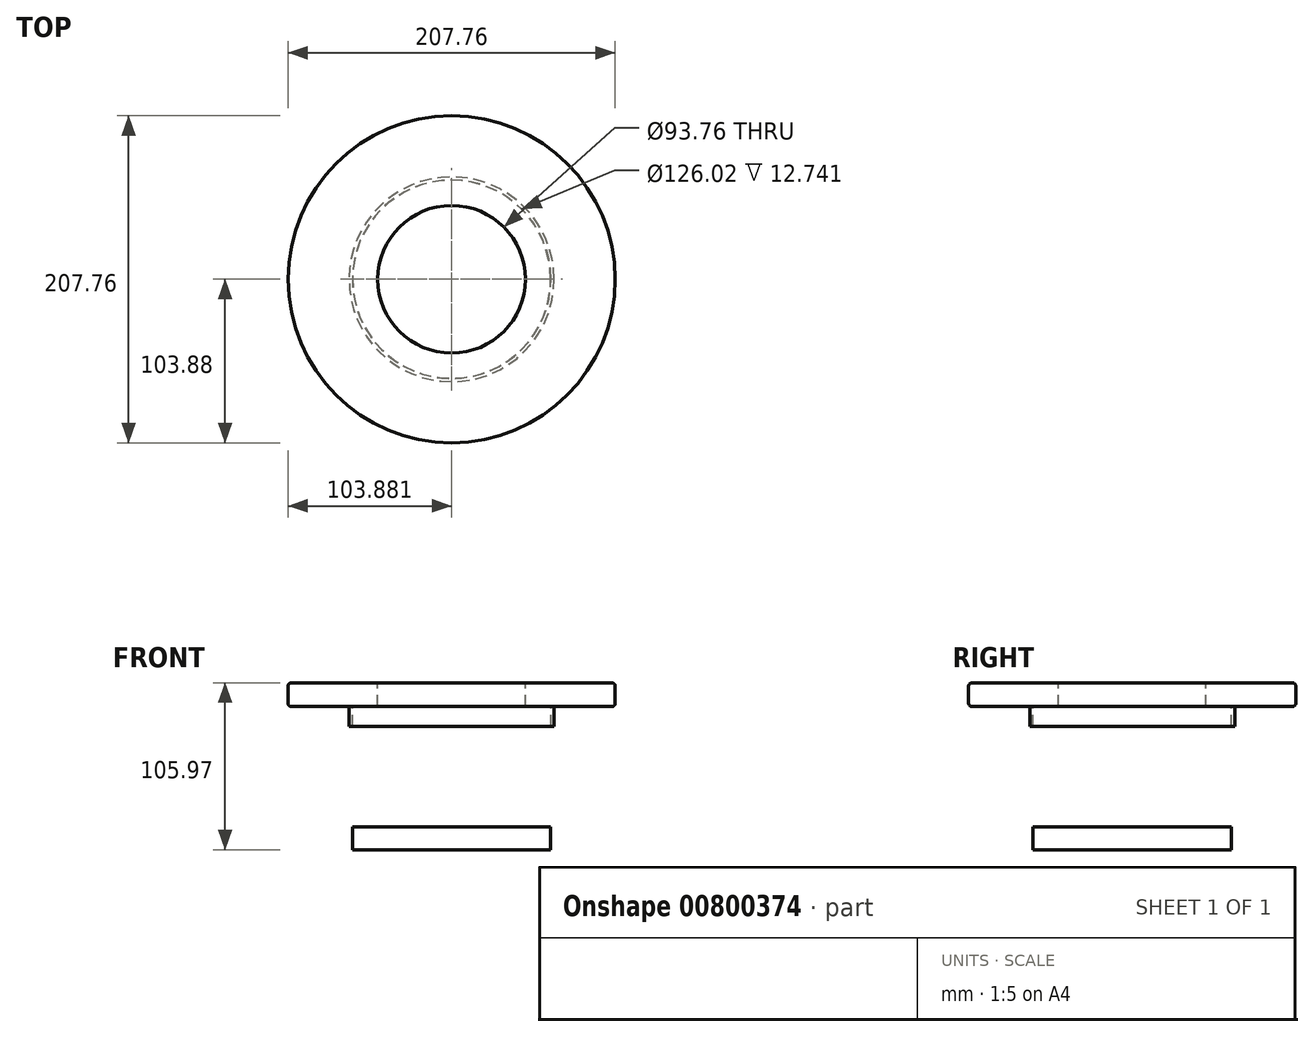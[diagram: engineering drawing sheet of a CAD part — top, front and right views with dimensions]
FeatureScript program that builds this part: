
annotation { "Feature Type Name" : "Feature", "Feature Type Description" : "" }
export const myFeature = defineFeature(function(context is Context, id is Id, definition is map)
    precondition{}
    {
        {
            var Q0;
            Q0=qCreatedBy(makeId("Front.planeOp"),FACE);
            var sketch = newSketch(context, id + "F0", { "sketchPlane" : qUnion([Q0])});
            skLineSegment(sketch, "E0.bottom", {"start": v(-44.86, 251.82) * mm, "end": v(-83.94, 251.82) * mm});
            skLineSegment(sketch, "E0.top", {"start": v(-44.86, 472.17) * mm, "end": v(-83.94, 472.17) * mm});
            skLineSegment(sketch, "E0.left", {"start": v(-44.86, 251.82) * mm, "end": v(-44.86, 472.17) * mm});
            skLineSegment(sketch, "E0.right", {"start": v(-83.94, 251.82) * mm, "end": v(-83.94, 472.17) * mm});
            skPoint(sketch, "E0.middle", {"position": v(-64.4, 362) * mm});
            skLineSegment(sketch, "E1.bottom", {"start": v(-7.4, 22.52) * mm, "end": v(-64.41, 22.52) * mm});
            skLineSegment(sketch, "E1.top", {"start": v(-7.4, 37.48) * mm, "end": v(-64.41, 37.48) * mm});
            skLineSegment(sketch, "E1.left", {"start": v(-7.4, 22.52) * mm, "end": v(-7.4, 37.48) * mm});
            skLineSegment(sketch, "E1.right", {"start": v(-64.41, 22.52) * mm, "end": v(-64.41, 37.48) * mm});
            skPoint(sketch, "E1.middle", {"position": v(-35.9, 30) * mm});
            skLineSegment(sketch, "E2.bottom", {"start": v(-7.4, 22.52) * mm, "end": v(-23.47, 22.52) * mm});
            skLineSegment(sketch, "E2.top", {"start": v(-7.4, -54.07) * mm, "end": v(-23.47, -54.07) * mm});
            skLineSegment(sketch, "E2.left", {"start": v(-7.4, 22.52) * mm, "end": v(-7.4, -54.07) * mm});
            skLineSegment(sketch, "E2.right", {"start": v(-23.47, 22.52) * mm, "end": v(-23.47, -54.07) * mm});
            skLineSegment(sketch, "E3.bottom", {"start": v(-23.47, -54.07) * mm, "end": v(39.47, -54.07) * mm});
            skLineSegment(sketch, "E3.top", {"start": v(-23.47, -68.49) * mm, "end": v(39.47, -68.49) * mm});
            skLineSegment(sketch, "E3.left", {"start": v(-23.47, -54.07) * mm, "end": v(-23.47, -68.49) * mm});
            skLineSegment(sketch, "E3.right", {"start": v(39.47, -54.07) * mm, "end": v(39.47, -68.49) * mm});
            skSolve(sketch);
        }
        {
            var Q0;
            Q0=qCreatedBy(makeId("Front.planeOp"),FACE);
            var sketch = newSketch(context, id + "F1", { "sketchPlane" : qUnion([Q0])});
            skLineSegment(sketch, "E4.bottom", {"start": v(-23.54, 22.5) * mm, "end": v(-25.61, 22.5) * mm});
            skLineSegment(sketch, "E4.top", {"start": v(-23.54, 9.76) * mm, "end": v(-25.61, 9.76) * mm});
            skLineSegment(sketch, "E4.left", {"start": v(-23.54, 22.5) * mm, "end": v(-23.54, 9.76) * mm});
            skLineSegment(sketch, "E4.right", {"start": v(-25.61, 22.5) * mm, "end": v(-25.61, 9.76) * mm});
            skSolve(sketch);
        }
        {
            var Q0;
            Q0=makeQuery(id+"F0.imprint","IMPRINT",FACE,{"disambiguationData":[TD([[makeQuery(id+"F0.imprint","IMPRINT",EDGE,{"derivedFrom":sQuery(id+"F0.wireOp",EDGE,"E1.bottom")}),-1.0]])]});
            var Q1;
            Q1=makeQuery(id+"F1.imprint","IMPRINT",FACE,{"disambiguationData":[TD([[makeQuery(id+"F1.imprint","IMPRINT",EDGE,{"derivedFrom":sQuery(id+"F1.wireOp",EDGE,"E4.bottom")}),1.0]])]});
            var Q2;
            Q2=makeQuery(id+"F0.imprint","IMPRINT",FACE,{"disambiguationData":[TD([[makeQuery(id+"F0.imprint","IMPRINT",EDGE,{"derivedFrom":sQuery(id+"F0.wireOp",EDGE,"E2.bottom")}),1.0]])]});
            var Q3;
            Q3=makeQuery(id+"F0.imprint","IMPRINT",FACE,{"disambiguationData":[TD([[makeQuery(id+"F0.imprint","IMPRINT",EDGE,{"derivedFrom":sQuery(id+"F0.wireOp",EDGE,"E3.top")}),1.0]])]});
            var Q4;
            Q4=sQuery(id+"F0.wireOp",EDGE,"E3.right");
            revolve(context, id + "F2", {"surfaceOperationType" : NewSurfaceOperationType.NEW, "entities" : qUnion([Q0, Q1, Q2, Q3]), "axis" : qUnion([Q4]), "revolveType" : RevolveType.FULL});
        }
        {
            var Q0;
            Q0=makeQuery(id+"F2.opRevolve","SWEPT_EDGE",EDGE,{"disambiguationData":[OSD([sQuery(id+"F0.wireOp",EDGE,"E1.bottom"),sQuery(id+"F0.wireOp",EDGE,"E1.right")])]});
            fillet(context, id + "F3", {"entities" : qUnion([Q0]), "radius" : 2 * mm, "tangentPropagation" : true, "allowEdgeOverflow" : false});
        }
        {
            var Q0;
            Q0=makeQuery(id+"F2.opRevolve","SWEPT_EDGE",EDGE,{"disambiguationData":[OSD([sQuery(id+"F0.wireOp",EDGE,"E1.top"),sQuery(id+"F0.wireOp",EDGE,"E1.right")])]});
            fillet(context, id + "F4", {"entities" : qUnion([Q0]), "radius" : 2 * mm, "tangentPropagation" : true, "allowEdgeOverflow" : false});
        }
    });
